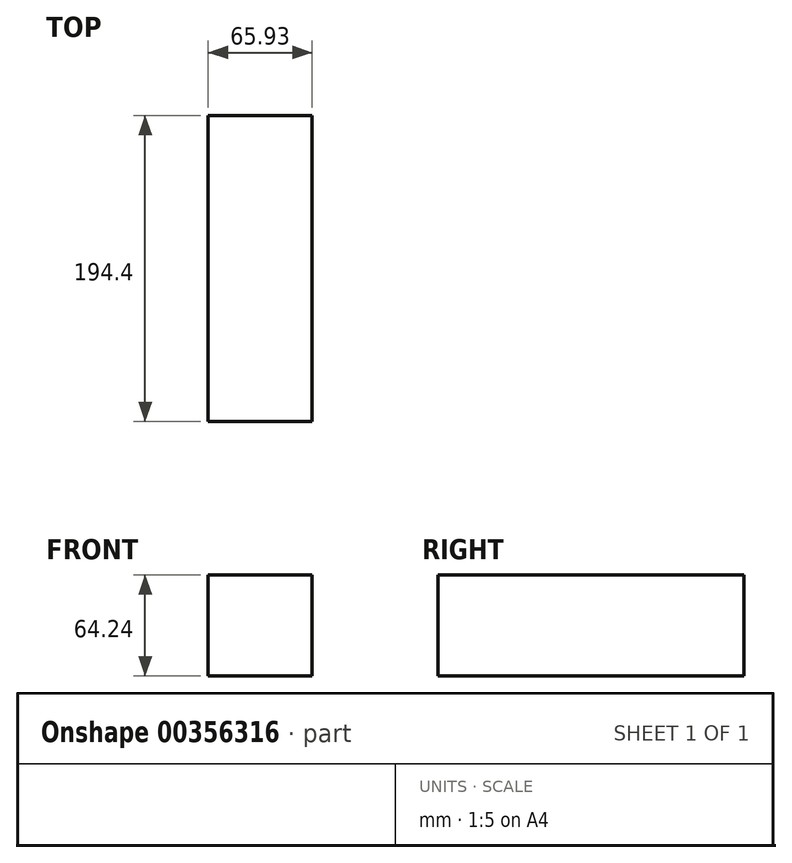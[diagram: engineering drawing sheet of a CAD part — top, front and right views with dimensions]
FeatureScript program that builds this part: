
annotation { "Feature Type Name" : "Feature", "Feature Type Description" : "" }
export const myFeature = defineFeature(function(context is Context, id is Id, definition is map)
    precondition{}
    {
        {
            var Q0;
            Q0=qCreatedBy(makeId("Front.planeOp"),FACE);
            var sketch = newSketch(context, id + "F0", { "sketchPlane" : qUnion([Q0])});
            skLineSegment(sketch, "E0.bottom", {"start": v(-28.7, 31.64) * mm, "end": v(37.24, 31.64) * mm});
            skLineSegment(sketch, "E0.top", {"start": v(-28.7, -32.6) * mm, "end": v(37.24, -32.6) * mm});
            skLineSegment(sketch, "E0.left", {"start": v(-28.7, 31.64) * mm, "end": v(-28.7, -32.6) * mm});
            skLineSegment(sketch, "E0.right", {"start": v(37.24, 31.64) * mm, "end": v(37.24, -32.6) * mm});
            skSolve(sketch);
        }
        {
            var Q0;
            Q0=makeQuery(id+"F0.imprint","IMPRINT",FACE,{"disambiguationData":[TD([[makeQuery(id+"F0.imprint","IMPRINT",EDGE,{"derivedFrom":sQuery(id+"F0.wireOp",EDGE,"E0.bottom")}),-1.0]])]});
            extrude(context, id + "F1", {"entities" : qUnion([Q0]), "depth" : 194.4 * mm});
        }
    });
